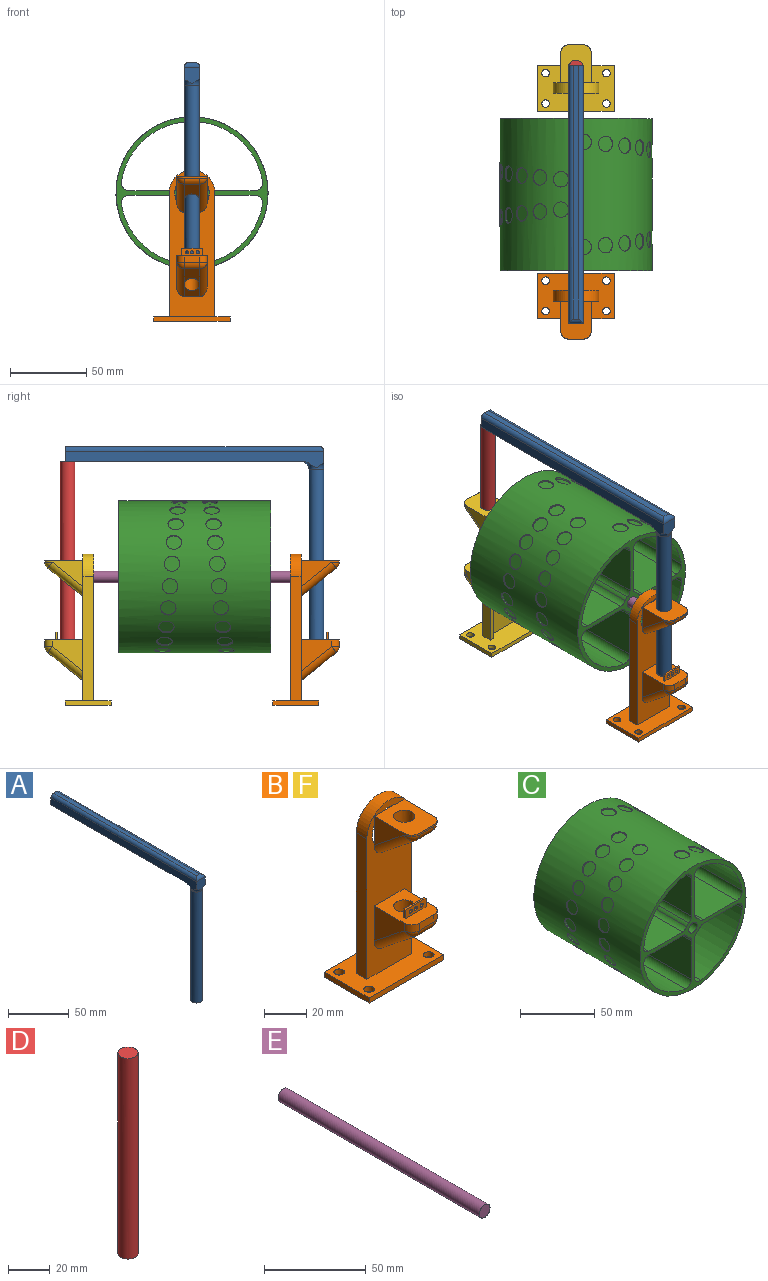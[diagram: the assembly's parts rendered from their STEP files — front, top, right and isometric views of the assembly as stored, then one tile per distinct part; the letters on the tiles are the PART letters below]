
ASSEMBLY  parts=6 mates=5
PART A: 12 faces, bbox 28.9x179.5x127.2 mm
  f0: plane 9.61x9.61mm, normal (0,0,-1), area 72.5mm2, adj f1
  f1: cylinder r=4.8mm len=112.23mm, axis (0,0,1), area 3387.1mm2, adj f0,f8
  f2: plane 10x9.93mm, normal (0,1,0), area 95.4mm2, adj f3,f5,f6,f7,f9,f10
  f3: plane 170x10.75mm, normal (-1,0,0), area 1214.6mm2, adj f2,f4,f7,f8,f9
  f4: plane 10.61x9.93mm, normal (0,-1,0), area 92.4mm2, adj f3,f5,f8,f11
  f5: plane 170x10.75mm, normal (1,0,0), area 1214.6mm2, adj f2,f4,f7,f8,f10
  f6: plane 167x3.93mm, normal (0,0,1), area 655.5mm2, adj f2,f9,f10,f11
  f7: plane 156.55x9.93mm, normal (0,0,-1), area 1544.6mm2, adj f2,f3,f5,f8
  f8: torus R=9.8mm, axis (0,0,1), area 138.4mm2, adj f1,f3,f4,f5,f7
  f9: cylinder r=3mm len=170mm, axis (0,1,0), area 796mm2, adj f2,f3,f6,f11
  f10: cylinder r=3mm len=170mm, axis (0,-1,0), area 796mm2, adj f2,f5,f6,f11
  f11: cylinder r=3mm len=9.93mm, axis (-1,0,0), area 36.5mm2, adj f4,f6,f9,f10
PART B: 57 faces, bbox 50x43.5x99.6 mm
  f0: plane 10x10mm, normal (0,-0.62,-0.78), area 77.8mm2, adj f2,f31,f42,f48
  f1: plane 10x10mm, normal (0,-0.62,-0.78), area 77.8mm2, adj f2,f32,f35,f41
  f2: plane 96.58x30mm, normal (0,-1,0), area 1802.6mm2, adj f0,f1,f4,f5,f6,f7,f9,f23
  f3: plane 96.58x30mm, normal (0,1,0), area 736.6mm2, adj f4,f5,f6,f7,f9,f14,f15,f16
  f4: plane 81.58x7mm, normal (1,0,0), area 571.1mm2, adj f2,f3,f5,f9
  f5: cylinder r=15mm len=30mm, axis (0,1,0), area 329.9mm2, adj f2,f3,f4,f6
  f6: plane 81.58x7mm, normal (-1,0,0), area 571.1mm2, adj f2,f3,f5,f9
  f7: cylinder r=11.35mm len=22.7mm, axis (0,1,0), area 499.2mm2, adj f2,f3,f22
  f8: plane 30x3mm, normal (1,0,0), area 90mm2, adj f9,f11,f12,f13
  f9: plane 50x30mm, normal (0,0,1), area 1307.5mm2, adj f2,f3,f4,f6,f8,f10,f12,f13
  f10: plane 30x3mm, normal (-1,0,0), area 90mm2, adj f9,f11,f12,f13
  f11: plane 50x30mm, normal (0,0,-1), area 1421.5mm2, adj f8,f10,f12,f13,f18,f19,f20,f21
  f12: plane 50x3mm, normal (0,-1,0), area 150mm2, adj f8,f9,f10,f11
  f13: plane 50x3mm, normal (0,1,0), area 150mm2, adj f8,f9,f10,f11
  f14: plane 73.71x4mm, normal (-1,0,0), area 294.9mm2, adj f3,f9,f16,f17
  f15: plane 73.71x4mm, normal (1,0,0), area 294.9mm2, adj f3,f9,f16,f17
  f16: cylinder r=14.35mm len=24mm, axis (0,1,0), area 113.7mm2, adj f3,f14,f15,f17
  f17: plane 73.71x24mm, normal (0,1,0), area 1659.6mm2, adj f9,f14,f15,f16
  f18: cylinder r=2.5mm len=5mm, axis (0,0,1), area 47.1mm2, adj f9,f11
  f19: cylinder r=2.5mm len=5mm, axis (0,0,1), area 47.1mm2, adj f9,f11
  f20: cylinder r=2.5mm len=5mm, axis (0,0,1), area 47.1mm2, adj f9,f11
  f21: cylinder r=2.5mm len=5mm, axis (0,0,1), area 47.1mm2, adj f9,f11
  f22: plane 22x20mm, normal (0,1,0), area 381.5mm2, adj f7,f23,f24,f25
  f23: plane 20x16.98mm, normal (1,0,0), area 179.5mm2, adj f2,f22,f24,f39,f41
  f24: plane 25x20mm, normal (0,0,1), area 410.7mm2, adj f2,f22,f23,f25,f26,f32,f36,f39
  f25: plane 20x16.98mm, normal (-1,0,0), area 179.5mm2, adj f2,f22,f24,f35,f36
  f26: plane 10x0.98mm, normal (0,-1,0), area 9.8mm2, adj f24,f36,f38,f39
  f27: plane 25x20mm, normal (0,0,1), area 394.5mm2, adj f2,f28,f29,f30,f31,f43,f46,f49
  f28: plane 20.35x20mm, normal (-1,0,0), area 246.9mm2, adj f2,f27,f42,f43
  f29: plane 20.35x20mm, normal (1,0,0), area 246.9mm2, adj f2,f27,f46,f48
  f30: plane 10x4.35mm, normal (0,-1,0), area 43.5mm2, adj f27,f43,f45,f46
  f31: cylinder r=5mm len=22.76mm, axis (0,0,1), area 589mm2, adj f0,f27,f33
  f32: cylinder r=5mm len=19.39mm, axis (0,0,1), area 483.1mm2, adj f1,f24,f34
  f33: plane 13.12x10.5mm, normal (0,-0.62,-0.78), area 117.8mm2, adj f31,f42,f45,f48
  f34: plane 13.12x10.5mm, normal (0,-0.62,-0.78), area 117.8mm2, adj f32,f35,f38,f41
  f35: cylinder r=5mm len=26.25mm, axis (0,-0.78,0.62), area 221.2mm2, adj f1,f2,f25,f34,f37
  f36: cylinder r=5mm len=5mm, axis (0,0,1), area 7.7mm2, adj f24,f25,f26,f37
  f37: sphere r=5mm, area 22.4mm2, adj f35,f36,f38
  f38: cylinder r=5mm len=10mm, axis (-1,0,0), area 44.8mm2, adj f26,f34,f37,f40
  f39: cylinder r=5mm len=5mm, axis (0,0,-1), area 7.7mm2, adj f23,f24,f26,f40
  f40: sphere r=5mm, area 22.4mm2, adj f38,f39,f41
  f41: cylinder r=5mm len=26.25mm, axis (0,-0.78,0.62), area 221.2mm2, adj f1,f2,f23,f34,f40
  f42: cylinder r=5mm len=26.25mm, axis (0,-0.78,0.62), area 221.2mm2, adj f0,f2,f28,f33,f44
  f43: cylinder r=5mm len=5mm, axis (0,0,1), area 34.1mm2, adj f27,f28,f30,f44
  f44: sphere r=5mm, area 22.4mm2, adj f42,f43,f45
  f45: cylinder r=5mm len=10mm, axis (-1,0,0), area 44.8mm2, adj f30,f33,f44,f47
  f46: cylinder r=5mm len=5mm, axis (0,0,-1), area 34.1mm2, adj f27,f29,f30,f47
  f47: sphere r=5mm, area 22.4mm2, adj f45,f46,f48
  f48: cylinder r=5mm len=26.25mm, axis (0,-0.78,0.62), area 221.2mm2, adj f0,f2,f29,f33,f47
  f49: plane 13.72x5mm, normal (0,1,0), area 59.2mm2, adj f27,f50,f52,f53,f54,f55,f56
  f50: plane 5x1.18mm, normal (-1,0,0), area 5.9mm2, adj f27,f49,f51,f53
  f51: plane 13.72x5mm, normal (0,-1,0), area 59.2mm2, adj f27,f50,f52,f53,f54,f55,f56
  f52: plane 5x1.18mm, normal (1,0,0), area 5.9mm2, adj f27,f49,f51,f53
  f53: plane 13.72x1.18mm, normal (0,0,1), area 16.3mm2, adj f49,f50,f51,f52
  f54: cylinder r=1mm len=2mm, axis (0,-1,0), area 7.4mm2, adj f49,f51
  f55: cylinder r=1mm len=2mm, axis (0,-1,0), area 7.4mm2, adj f49,f51
  f56: cylinder r=1mm len=2mm, axis (0,-1,0), area 7.4mm2, adj f49,f51
PART C: 120 faces, bbox 100.6x100x100.6 mm
  f0: plane 100x100mm, normal (0,1,0), area 1566.5mm2, adj f1,f2,f88,f89,f90,f91,f92,f93
  f1: cylinder r=50mm len=100mm, axis (0,1,0), area 27973.1mm2, adj f0,f3,f4,f6,f8,f10,f12,f14
  f2: cylinder r=4mm len=100mm, axis (0,1,0), area 2513.3mm2, adj f0,f3
  f3: plane 100x100mm, normal (0,-1,0), area 1566.5mm2, adj f1,f2,f88,f89,f90,f91,f92,f93
  f4: cylinder r=5.1mm len=10.22mm, axis (-0.2,-0.02,0.98), area 28.5mm2, adj f1,f5
  f5: plane 10.2x9.99mm, normal (-0.2,-0.02,0.98), area 81.7mm2, adj f4
  f6: cylinder r=5.1mm len=10.26mm, axis (0.1,-0.02,0.99), area 28.2mm2, adj f1,f7
  f7: plane 10.2x10.15mm, normal (0.1,-0.02,0.99), area 81.7mm2, adj f6
  f8: cylinder r=5.1mm len=10.22mm, axis (0.39,-0.02,0.92), area 28mm2, adj f1,f9
  f9: plane 10.2x9.39mm, normal (0.39,-0.02,0.92), area 81.7mm2, adj f8
  f10: cylinder r=5.1mm len=10.22mm, axis (0.64,-0.02,0.77), area 28.1mm2, adj f1,f11
  f11: plane 10.2x7.81mm, normal (0.64,-0.02,0.77), area 81.7mm2, adj f10
  f12: cylinder r=5.1mm len=10.22mm, axis (0.84,-0.02,0.54), area 28.1mm2, adj f1,f13
  f13: plane 10.2x8.58mm, normal (0.84,-0.02,0.54), area 81.7mm2, adj f12
  f14: cylinder r=5.1mm len=10.22mm, axis (0.96,-0.02,0.27), area 28.1mm2, adj f1,f15
  f15: plane 10.2x9.82mm, normal (0.96,-0.02,0.27), area 81.7mm2, adj f14
  f16: cylinder r=5.1mm len=10.23mm, axis (1,-0.02,-0.03), area 28mm2, adj f1,f17
  f17: plane 10.2x10.2mm, normal (1,-0.02,-0.03), area 81.7mm2, adj f16
  f18: cylinder r=5.1mm len=10.22mm, axis (0.95,-0.02,-0.32), area 28.1mm2, adj f1,f19
  f19: plane 10.2x9.67mm, normal (0.95,-0.02,-0.32), area 81.7mm2, adj f18
  f20: cylinder r=5.1mm len=10.22mm, axis (0.81,-0.02,-0.58), area 28.2mm2, adj f1,f21
  f21: plane 10.2x8.28mm, normal (0.81,-0.02,-0.58), area 81.7mm2, adj f20
  f22: cylinder r=5.1mm len=10.22mm, axis (0.6,-0.02,-0.8), area 28.1mm2, adj f1,f23
  f23: plane 10.2x8.13mm, normal (0.6,-0.02,-0.8), area 81.7mm2, adj f22
  f24: cylinder r=5.1mm len=10.22mm, axis (0.34,-0.02,-0.94), area 28mm2, adj f1,f25
  f25: plane 10.2x9.59mm, normal (0.34,-0.02,-0.94), area 81.7mm2, adj f24
  f26: cylinder r=5.1mm len=10.24mm, axis (0.05,-0.02,-1), area 28mm2, adj f1,f27
  f27: plane 10.2x10.19mm, normal (0.05,-0.02,-1), area 81.7mm2, adj f26
  f28: cylinder r=5.1mm len=10.22mm, axis (-0.25,-0.02,-0.97), area 28.1mm2, adj f1,f29
  f29: plane 10.2x9.89mm, normal (-0.25,-0.02,-0.97), area 81.7mm2, adj f28
  f30: cylinder r=5.1mm len=10.22mm, axis (-0.52,-0.02,-0.85), area 28.1mm2, adj f1,f31
  f31: plane 10.2x8.71mm, normal (-0.52,-0.02,-0.85), area 81.7mm2, adj f30
  f32: cylinder r=5.1mm len=10.22mm, axis (-0.75,-0.02,-0.66), area 28.1mm2, adj f1,f33
  f33: plane 10.2x7.65mm, normal (-0.75,-0.02,-0.66), area 81.7mm2, adj f32
  f34: cylinder r=5.1mm len=10.22mm, axis (-0.91,-0.02,-0.41), area 28mm2, adj f1,f35
  f35: plane 10.2x9.3mm, normal (-0.91,-0.02,-0.41), area 81.7mm2, adj f34
  f36: cylinder r=5.1mm len=10.26mm, axis (-0.99,-0.02,-0.12), area 28mm2, adj f1,f37
  f37: plane 10.2x10.12mm, normal (-0.99,-0.02,-0.12), area 81.7mm2, adj f36
  f38: cylinder r=5.1mm len=10.24mm, axis (-0.98,-0.02,0.17), area 28.1mm2, adj f1,f39
  f39: plane 10.2x10.05mm, normal (-0.98,-0.02,0.17), area 81.7mm2, adj f38
  f40: cylinder r=5.1mm len=10.22mm, axis (-0.89,-0.02,0.45), area 28.1mm2, adj f1,f41
  f41: plane 10.2x9.08mm, normal (-0.89,-0.02,0.45), area 81.7mm2, adj f40
  f42: cylinder r=5.1mm len=10.22mm, axis (-0.72,-0.02,0.7), area 28.1mm2, adj f1,f43
  f43: plane 10.2x7.31mm, normal (-0.72,-0.02,0.7), area 81.7mm2, adj f42
  f44: cylinder r=5.1mm len=10.22mm, axis (-0.48,-0.02,0.88), area 28.1mm2, adj f1,f45
  f45: plane 10.2x8.95mm, normal (-0.48,-0.02,0.88), area 81.7mm2, adj f44
  f46: cylinder r=5.1mm len=10.22mm, axis (-0.2,0.02,0.98), area 28.5mm2, adj f1,f47
  f47: plane 10.2x9.99mm, normal (-0.2,0.02,0.98), area 81.7mm2, adj f46
  f48: cylinder r=5.1mm len=10.26mm, axis (0.1,0.02,0.99), area 28.2mm2, adj f1,f49
  f49: plane 10.2x10.15mm, normal (0.1,0.02,0.99), area 81.7mm2, adj f48
  f50: cylinder r=5.1mm len=10.22mm, axis (0.39,0.02,0.92), area 28.1mm2, adj f1,f51
  f51: plane 10.2x9.39mm, normal (0.39,0.02,0.92), area 81.7mm2, adj f50
  f52: cylinder r=5.1mm len=10.22mm, axis (0.64,0.02,0.77), area 28.2mm2, adj f1,f53
  f53: plane 10.2x7.81mm, normal (0.64,0.02,0.77), area 81.7mm2, adj f52
  f54: cylinder r=5.1mm len=10.22mm, axis (0.84,0.02,0.54), area 28.1mm2, adj f1,f55
  f55: plane 10.2x8.58mm, normal (0.84,0.02,0.54), area 81.7mm2, adj f54
  f56: cylinder r=5.1mm len=10.22mm, axis (0.96,0.02,0.27), area 28.1mm2, adj f1,f57
  f57: plane 10.2x9.82mm, normal (0.96,0.02,0.27), area 81.7mm2, adj f56
  f58: cylinder r=5.1mm len=10.23mm, axis (1,0.02,-0.03), area 28mm2, adj f1,f59
  f59: plane 10.2x10.2mm, normal (1,0.02,-0.03), area 81.7mm2, adj f58
  f60: cylinder r=5.1mm len=10.22mm, axis (0.95,0.02,-0.32), area 28.1mm2, adj f1,f61
  f61: plane 10.2x9.67mm, normal (0.95,0.02,-0.32), area 81.7mm2, adj f60
  f62: cylinder r=5.1mm len=10.22mm, axis (0.81,0.02,-0.58), area 28.2mm2, adj f1,f63
  f63: plane 10.2x8.28mm, normal (0.81,0.02,-0.58), area 81.7mm2, adj f62
  f64: cylinder r=5.1mm len=10.22mm, axis (0.6,0.02,-0.8), area 28.1mm2, adj f1,f65
  f65: plane 10.2x8.13mm, normal (0.6,0.02,-0.8), area 81.7mm2, adj f64
  f66: cylinder r=5.1mm len=10.22mm, axis (0.34,0.02,-0.94), area 28mm2, adj f1,f67
  f67: plane 10.2x9.59mm, normal (0.34,0.02,-0.94), area 81.7mm2, adj f66
  f68: cylinder r=5.1mm len=10.24mm, axis (0.05,0.02,-1), area 28mm2, adj f1,f69
  f69: plane 10.2x10.19mm, normal (0.05,0.02,-1), area 81.7mm2, adj f68
  f70: cylinder r=5.1mm len=10.22mm, axis (-0.25,0.02,-0.97), area 28.1mm2, adj f1,f71
  f71: plane 10.2x9.89mm, normal (-0.25,0.02,-0.97), area 81.7mm2, adj f70
  f72: cylinder r=5.1mm len=10.22mm, axis (-0.52,0.02,-0.85), area 28.1mm2, adj f1,f73
  f73: plane 10.2x8.71mm, normal (-0.52,0.02,-0.85), area 81.7mm2, adj f72
  f74: cylinder r=5.1mm len=10.22mm, axis (-0.75,0.02,-0.66), area 28.1mm2, adj f1,f75
  f75: plane 10.2x7.65mm, normal (-0.75,0.02,-0.66), area 81.7mm2, adj f74
  f76: cylinder r=5.1mm len=10.22mm, axis (-0.91,0.02,-0.41), area 28mm2, adj f1,f77
  f77: plane 10.2x9.3mm, normal (-0.91,0.02,-0.41), area 81.7mm2, adj f76
  f78: cylinder r=5.1mm len=10.26mm, axis (-0.99,0.02,-0.12), area 28mm2, adj f1,f79
  f79: plane 10.2x10.12mm, normal (-0.99,0.02,-0.12), area 81.7mm2, adj f78
  f80: cylinder r=5.1mm len=10.24mm, axis (-0.98,0.02,0.17), area 28.1mm2, adj f1,f81
  f81: plane 10.2x10.05mm, normal (-0.98,0.02,0.17), area 81.7mm2, adj f80
  f82: cylinder r=5.1mm len=10.22mm, axis (-0.89,0.02,0.45), area 28.1mm2, adj f1,f83
  f83: plane 10.2x9.08mm, normal (-0.89,0.02,0.45), area 81.7mm2, adj f82
  f84: cylinder r=5.1mm len=10.22mm, axis (-0.72,0.02,0.7), area 28.1mm2, adj f1,f85
  f85: plane 10.2x7.31mm, normal (-0.72,0.02,0.7), area 81.7mm2, adj f84
  f86: cylinder r=5.1mm len=10.22mm, axis (-0.48,0.02,0.88), area 28.1mm2, adj f1,f87
  f87: plane 10.2x8.95mm, normal (-0.48,0.02,0.88), area 81.7mm2, adj f86
  f88: cylinder r=7mm len=100mm, axis (0,1,0), area 298.2mm2, adj f0,f3,f93,f95
  f89: cylinder r=47mm len=100mm, axis (0,1,0), area 5922.1mm2, adj f0,f3,f92,f94
  f90: plane 100x31.41mm, normal (1,0,0), area 3140.7mm2, adj f0,f3,f94,f95
  f91: plane 100x31.41mm, normal (0,0,1), area 3140.7mm2, adj f0,f3,f92,f93
  f92: cylinder r=5mm len=100mm, axis (0,1,0), area 863.1mm2, adj f0,f3,f89,f91
  f93: cylinder r=5mm len=100mm, axis (0,1,0), area 499.2mm2, adj f0,f3,f88,f91
  f94: cylinder r=5mm len=100mm, axis (0,1,0), area 863.1mm2, adj f0,f3,f89,f90
  f95: cylinder r=5mm len=100mm, axis (0,1,0), area 499.2mm2, adj f0,f3,f88,f90
  f96: cylinder r=47mm len=100mm, axis (0,1,0), area 5922.1mm2, adj f0,f3,f100,f102
  f97: cylinder r=7mm len=100mm, axis (0,1,0), area 298.2mm2, adj f0,f3,f101,f103
  f98: plane 100x31.41mm, normal (0,0,1), area 3140.7mm2, adj f0,f3,f102,f103
  f99: plane 100x31.41mm, normal (-1,0,0), area 3140.7mm2, adj f0,f3,f100,f101
  f100: cylinder r=5mm len=100mm, axis (0,1,0), area 863.1mm2, adj f0,f3,f96,f99
  f101: cylinder r=5mm len=100mm, axis (0,1,0), area 499.2mm2, adj f0,f3,f97,f99
  f102: cylinder r=5mm len=100mm, axis (0,1,0), area 863.1mm2, adj f0,f3,f96,f98
  f103: cylinder r=5mm len=100mm, axis (0,1,0), area 499.2mm2, adj f0,f3,f97,f98
  f104: plane 100x31.41mm, normal (-1,0,0), area 3140.7mm2, adj f0,f3,f110,f111
  f105: cylinder r=47mm len=100mm, axis (0,1,0), area 5922.1mm2, adj f0,f3,f108,f110
  f106: cylinder r=7mm len=100mm, axis (0,1,0), area 298.2mm2, adj f0,f3,f109,f111
  f107: plane 100x31.41mm, normal (0,0,-1), area 3140.7mm2, adj f0,f3,f108,f109
  f108: cylinder r=5mm len=100mm, axis (0,1,0), area 863.1mm2, adj f0,f3,f105,f107
  f109: cylinder r=5mm len=100mm, axis (0,1,0), area 499.2mm2, adj f0,f3,f106,f107
  f110: cylinder r=5mm len=100mm, axis (0,1,0), area 863.1mm2, adj f0,f3,f104,f105
  f111: cylinder r=5mm len=100mm, axis (0,1,0), area 499.2mm2, adj f0,f3,f104,f106
  f112: cylinder r=47mm len=100mm, axis (0,1,0), area 5922.1mm2, adj f0,f3,f116,f118
  f113: cylinder r=7mm len=100mm, axis (0,1,0), area 298.2mm2, adj f0,f3,f117,f119
  f114: plane 100x31.41mm, normal (0,0,-1), area 3140.7mm2, adj f0,f3,f118,f119
  f115: plane 100x31.41mm, normal (1,0,0), area 3140.7mm2, adj f0,f3,f116,f117
  f116: cylinder r=5mm len=100mm, axis (0,1,0), area 863.1mm2, adj f0,f3,f112,f115
  f117: cylinder r=5mm len=100mm, axis (0,1,0), area 499.2mm2, adj f0,f3,f113,f115
  f118: cylinder r=5mm len=100mm, axis (0,1,0), area 863.1mm2, adj f0,f3,f112,f114
  f119: cylinder r=5mm len=100mm, axis (0,1,0), area 499.2mm2, adj f0,f3,f113,f114
PART D: 3 faces, bbox 9.6x9.6x117.2 mm
  f0: plane 9.61x9.61mm, normal (0,0,-1), area 72.5mm2, adj f1
  f1: cylinder r=4.8mm len=117.23mm, axis (0,0,1), area 3538mm2, adj f0,f2
  f2: plane 9.61x9.61mm, normal (0,0,1), area 72.5mm2, adj f1
PART E: 3 faces, bbox 7.5x140x7.5 mm
  f0: cylinder r=3.75mm len=140mm, axis (0,1,0), area 3298.7mm2, adj f1,f2
  f1: plane 7.5x7.5mm, normal (0,-1,0), area 44.2mm2, adj f0
  f2: plane 7.5x7.5mm, normal (0,1,0), area 44.2mm2, adj f0
PART F: same geometry as B
PLACE A t=(0,37.43,5.51)mm
PLACE B t=(0,-116.5,-34.58)mm
PLACE C at identity
PLACE D rot(axis=(0,0,1),180deg) t=(0,20.07,5.51)mm
PLACE E t=(0,20,0)mm
PLACE F rot(axis=(0,0,1),180deg) t=(0,20,-34.58)mm
MATE revolute B.f5 <-> E.f0  axis (0,-1,0) through (0,-120,0)mm
MATE slider A.f1 <-> B.f31  axis (0,0,-1) through (0,-130,-41.49)mm
MATE revolute F.f5 <-> E.f0  axis (0,-1,0) through (0,20,0)mm
MATE cylindrical E.f0 <-> C.f1  axis (0,-1,0) through (0,-120,0)mm
MATE slider D.f1 <-> F.f31  axis (0,0,1) through (0,33.5,-41.49)mm
